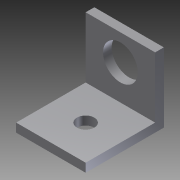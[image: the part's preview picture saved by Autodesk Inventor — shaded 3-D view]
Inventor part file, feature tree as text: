
AUTODESK INVENTOR PART (.ipt)
format: ipt  version: 2012 (Build 160160000, 160)  size: 99,840 bytes
history: native  units: in
note: dims shown in document units (in); Inventor stores cm internally (conversion verified against a paired STEP export)
features: extrude x3, sketch x3
ambient origin geometry x8: Origin, YZ Plane, XZ Plane, XY Plane, X Axis, Y Axis, Z Axis, Center Point
bodies: Solid1 (feature_tree)
feature tree (6):
  extrude  "Extrusion1"  Depth=1.0in
  extrude  "Extrusion2"  Depth=0.125in TaperAngle=0.0deg
  extrude  "Extrusion3"  Depth=1.0in TaperAngle=0.0deg
  sketch  "Sketch1"  dims[d0=1.0in d1=1.0in]
  sketch  "Sketch2"  dims[d2=0.5in d3=0.125in d4=0.0in]
  sketch  "Sketch3"  dims[d5=0.125in d6=1.0in d7=0.0in d9=0.25in d11=0.5in d13=0.5in d14=1.0in d15=0.0in d16=0.375in]
